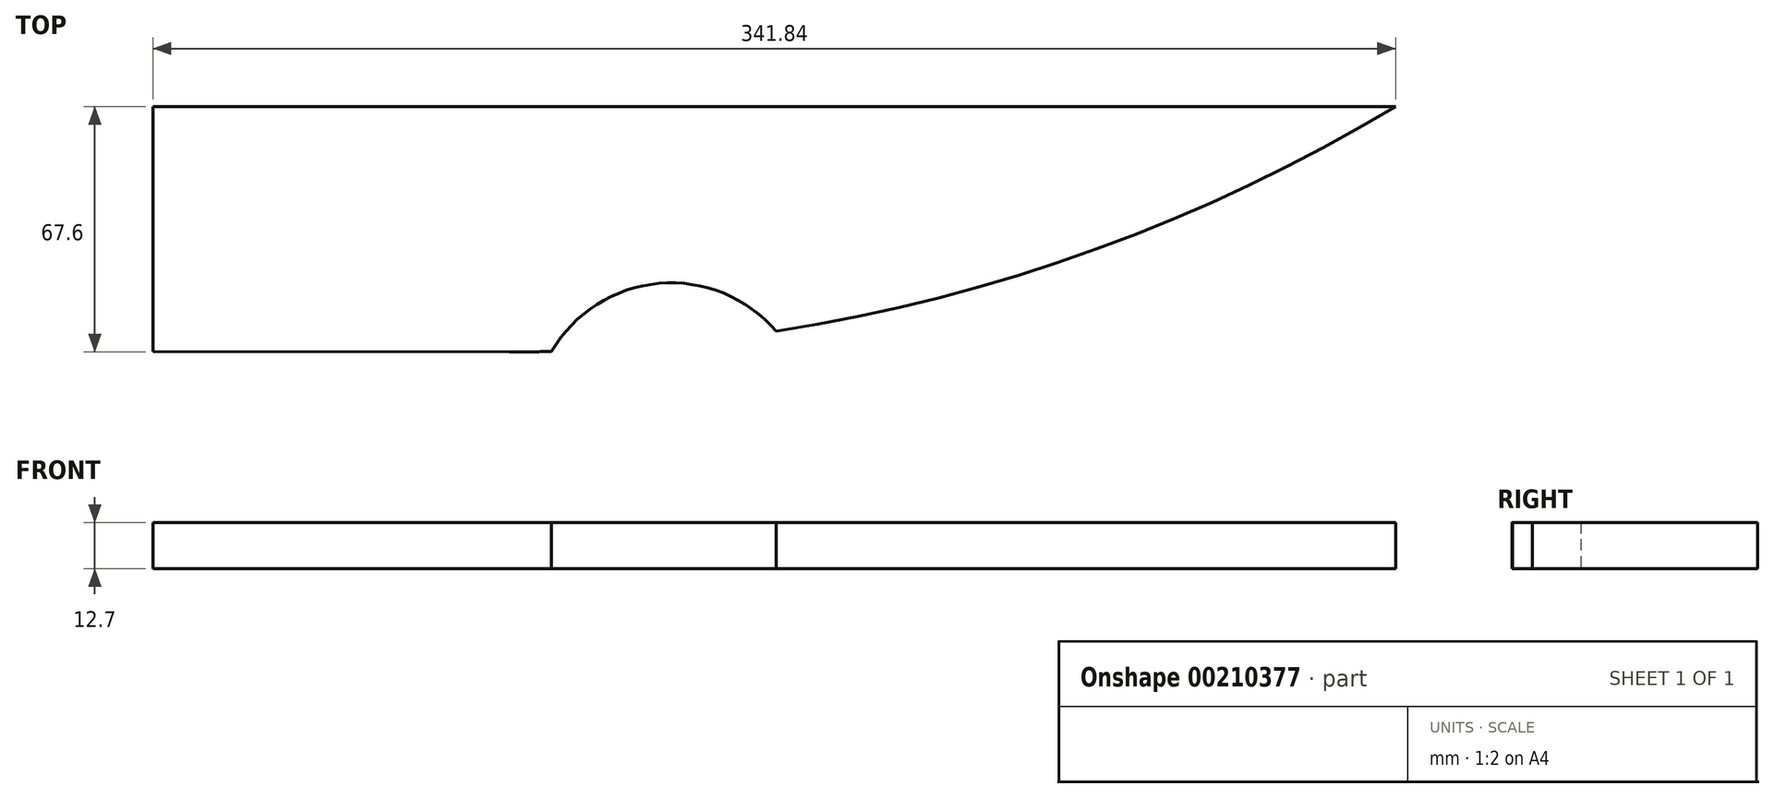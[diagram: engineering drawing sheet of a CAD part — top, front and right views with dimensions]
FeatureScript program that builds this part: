
annotation { "Feature Type Name" : "Feature", "Feature Type Description" : "" }
export const myFeature = defineFeature(function(context is Context, id is Id, definition is map)
    precondition{}
    {
        {
            assignVariable(context, id + "F0", {"name" : "r", "anyValue" : 2.5});
        }
        {
            var Q0;
            Q0=qCreatedBy(makeId("Top.planeOp"),FACE);
            var sketch = newSketch(context, id + "F1", { "sketchPlane" : qUnion([Q0])});
            skArc(sketch, "E0", {"start": v(0, 0) * mm, "mid": v(126.53, 17.16) * mm, "end": v(243.83, 67.6) * mm});
            skLineSegment(sketch, "E1", {"start": v(0, 0) * mm, "end": v(-98, 0.09) * mm});
            skLineSegment(sketch, "E2", {"start": v(243.83, 67.6) * mm, "end": v(-98, 67.6) * mm});
            skLineSegment(sketch, "E3", {"start": v(-98, 67.6) * mm, "end": v(-98, 0.09) * mm});
            skSolve(sketch);
        }
        {
            var Q0;
            Q0=qCreatedBy(makeId("Right.planeOp"),FACE);
            var Q1;
            Q1=sQuery(id+"F1.wireOp",VERTEX,"E0.center");
            cPlane(context, id + "F2", {"entities" : qUnion([Q0, Q1]), "cplaneType" : CPlaneType.PLANE_POINT, "offset" : 25.4 * mm, "width" : 152.4 * mm, "height" : 152.4 * mm});
        }
        {
            var Q0;
            Q0=qCreatedBy(id+"F2.planeOp",FACE);
            var sketch = newSketch(context, id + "F3", { "sketchPlane" : qUnion([Q0])});
            skLineSegment(sketch, "E4", {"start": v(472, 0) * mm, "end": v(472, 136.56) * mm});
            skSolve(sketch);
        }
        {
            var Q0;
            Q0=qCreatedBy(makeId("Top.planeOp"),FACE);
            var sketch = newSketch(context, id + "F4", { "sketchPlane" : qUnion([Q0])});
            skLineSegment(sketch, "E5", {"start": v(0.43, 472) * mm, "end": v(42.64, 1.9) * mm, "construction": true});
            skLineSegment(sketch, "E6", {"start": v(11.02, -0.95) * mm, "end": v(74.27, 4.73) * mm});
            skArc(sketch, "E7", {"start": v(74.27, 4.73) * mm, "mid": v(41.12, 18.86) * mm, "end": v(11.02, -0.95) * mm});
            skSolve(sketch);
        }
        {
            assignVariable(context, id + "F5", {"name" : "r", "anyValue" : getVariable(context, 'r') - .5});
        }
        {
            var Q0;
            Q0=makeQuery(id+"F1.imprint","IMPRINT",FACE,{"disambiguationData":[TD([[makeQuery(id+"F1.imprint","IMPRINT",EDGE,{"derivedFrom":sQuery(id+"F1.wireOp",EDGE,"E0")}),1.0]])]});
            extrude(context, id + "F6", {"entities" : qUnion([Q0]), "depth" : 12.7 * mm});
        }
        {
            var Q0;
            Q0=qSketchRegion(id+"F4",true);
            var Q1;
            Q1=makeQuery(id+"FD4SDvpFnBh91px_0.1.F4.imprint","IMPRINT",FACE,{"disambiguationData":[TD([[makeQuery(id+"FD4SDvpFnBh91px_0.1.F4.imprint","IMPRINT",EDGE,{"derivedFrom":sQuery(id+"FD4SDvpFnBh91px_0.1.F4.wireOp",EDGE,"E6")}),1.0]])]});
            var Q2;
            Q2=makeQuery(id+"FD4SDvpFnBh91px_0.2.F4.imprint","IMPRINT",FACE,{"disambiguationData":[TD([[makeQuery(id+"FD4SDvpFnBh91px_0.2.F4.imprint","IMPRINT",EDGE,{"derivedFrom":sQuery(id+"FD4SDvpFnBh91px_0.2.F4.wireOp",EDGE,"E6")}),1.0]])]});
            extrude(context, id + "F7", {"entities" : qUnion([Q0, Q1, Q2]), "operationType" : NewBodyOperationType.REMOVE, "depth" : 25.4 * mm});
        }
    });
